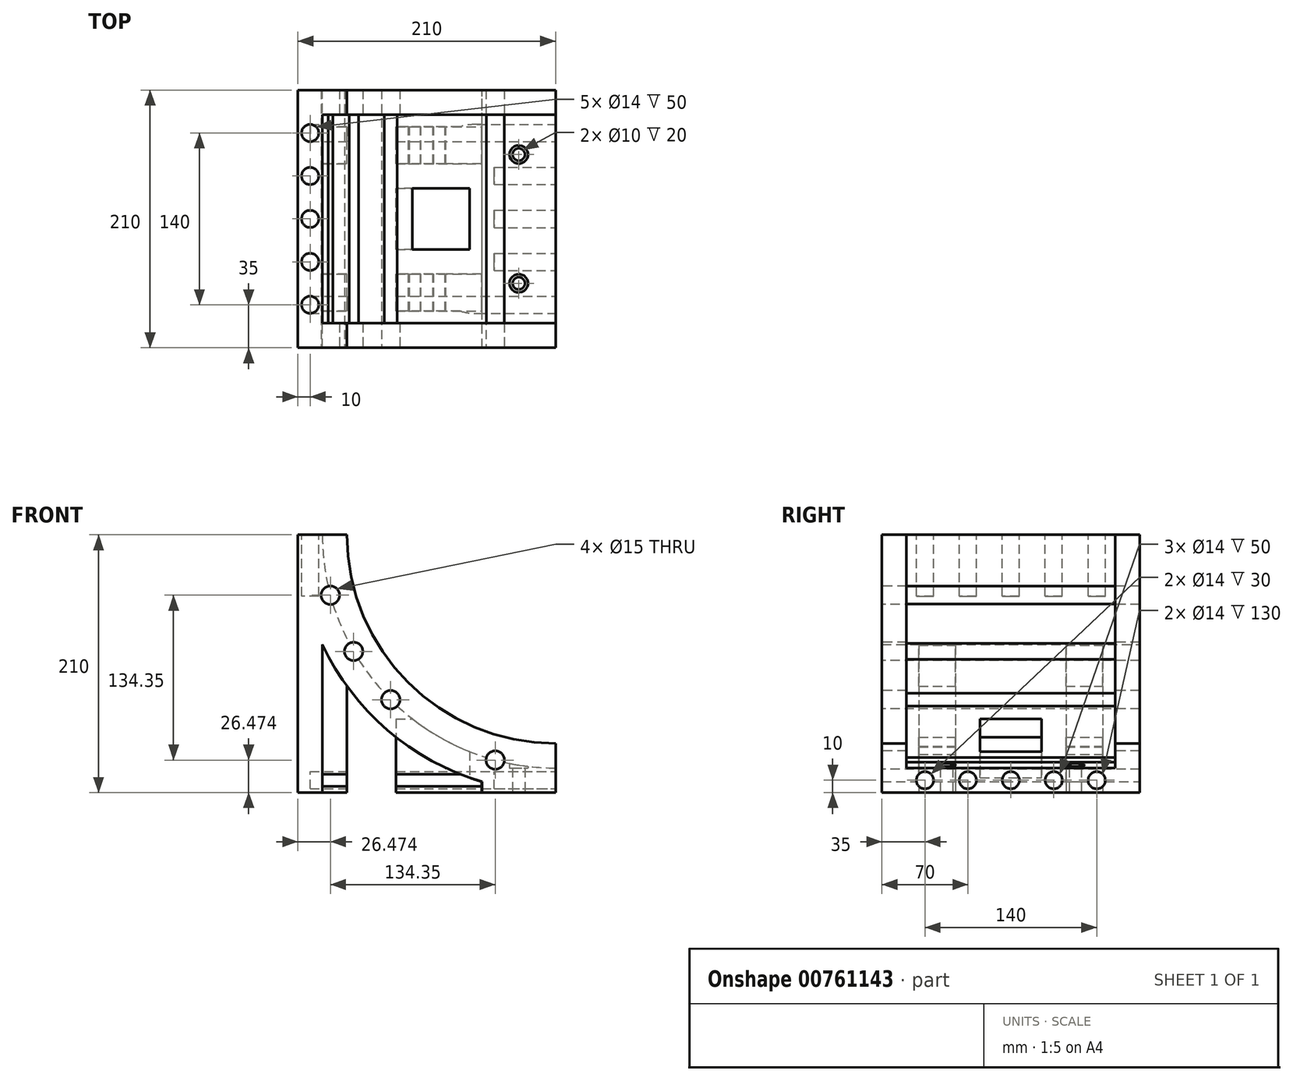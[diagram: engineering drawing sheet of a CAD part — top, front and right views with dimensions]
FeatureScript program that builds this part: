
annotation { "Feature Type Name" : "Feature", "Feature Type Description" : "" }
export const myFeature = defineFeature(function(context is Context, id is Id, definition is map)
    precondition{}
    {
        {
            var Q0;
            Q0=qCreatedBy(makeId("Front.planeOp"),FACE);
            var sketch = newSketch(context, id + "F0", { "sketchPlane" : qUnion([Q0])});
            skCircle(sketch, "E0", {"center": v(0, 0) * mm, "radius": 210 * mm});
            skCircle(sketch, "E1", {"center": v(0, 0) * mm, "radius": 190 * mm});
            skLineSegment(sketch, "E2", {"start": v(0, 0) * mm, "end": v(-210, 0) * mm});
            skLineSegment(sketch, "E3", {"start": v(0, 0) * mm, "end": v(0, -210) * mm});
            skSolve(sketch);
        }
        {
            var Q0;
            {var subQ0=sQuery(id+"F0.wireOp",EDGE,"E2");var subQ1=sQuery(id+"F0.wireOp",EDGE,"E0");var subQ2=makeQuery(id+"F0.imprint","INTERSECT",VERTEX,{"derivedFrom":[subQ1,subQ0]});Q0=makeQuery(id+"F0.imprint","IMPRINT",FACE,{"disambiguationData":[TD([[makeQuery(id+"F0.imprint","IMPRINT",EDGE,{"disambiguationData":[TD([[subQ2,-1.0]])],"derivedFrom":subQ1}),1.0]])]});}
            extrude(context, id + "F1", {"entities" : qUnion([Q0]), "depth" : 210 * mm, "offsetDistance" : 25 * mm});
        }
        {
            var Q0;
            Q0=makeQuery(id+"F1.opExtrude","SWEPT_FACE",FACE,{"disambiguationData":[OSD([sQuery(id+"F0.wireOp",EDGE,"E2")])]});
            extrude(context, id + "F2", {"entities" : qUnion([Q0]), "operationType" : NewBodyOperationType.ADD, "oppositeDirection" : true, "depth" : 210 * mm, "offsetDistance" : 25 * mm});
        }
        {
            var Q0;
            Q0=makeQuery(id+"F1.opExtrude","SWEPT_FACE",FACE,{"disambiguationData":[OSD([sQuery(id+"F0.wireOp",EDGE,"E3")])]});
            extrude(context, id + "F3", {"entities" : qUnion([Q0]), "operationType" : NewBodyOperationType.ADD, "oppositeDirection" : true, "depth" : 60 * mm, "offsetDistance" : 25 * mm});
        }
        {
            var Q0;
            Q0=makeQuery(id+"F3.opExtrude","SWEPT_FACE",FACE,{"disambiguationData":[OSD([sQuery(id+"F0.wireOp",EDGE,"E0"),sQuery(id+"F0.wireOp",EDGE,"E3")])]});
            var sketch = newSketch(context, id + "F4", { "sketchPlane" : qUnion([Q0])});
            skLineSegment(sketch, "E4", {"start": v(-30, 210) * mm, "end": v(-30, 0) * mm});
            skLineSegment(sketch, "E5", {"start": v(0, 157.5) * mm, "end": v(-60, 157.5) * mm});
            skLineSegment(sketch, "E6", {"start": v(-60, 52.5) * mm, "end": v(0, 52.5) * mm});
            skPoint(sketch, "E7", {"position": v(-30, 157.5) * mm});
            skPoint(sketch, "E8", {"position": v(-30, 52.5) * mm});
            skSolve(sketch);
        }
        {
            var Q0;
            Q0=sQuery(id+"F4.wireOp",VERTEX,"E7");
            var Q1;
            Q1=sQuery(id+"F4.wireOp",VERTEX,"E8");
            var Q2;
            Q2=makeQuery(id+"F1.opExtrude","SWEPT_BODY",BODY,{"disambiguationData":[OSD([sQuery(id+"F0.wireOp",EDGE,"E0"),sQuery(id+"F0.wireOp",EDGE,"E1"),sQuery(id+"F0.wireOp",EDGE,"E2"),sQuery(id+"F0.wireOp",EDGE,"E3")])]});
            hole(context, id + "F5", {"style" : HoleStyle.SIMPLE, "endStyle" : HoleEndStyle.BLIND, "holeDiameter" : 15 * mm, "majorDiameter" : 5 * mm, "holeDepth" : 40 * mm, "isTappedThrough" : true, "tappedDepth" : 12 * mm, "tapClearance" : 3, "startFromSketch" : true, "locations" : qUnion([Q0, Q1]), "scope" : qUnion([Q2])});
        }
        {
            var Q0;
            {var subQ0=sQuery(id+"F0.wireOp",EDGE,"E3");var subQ1=sQuery(id+"F0.wireOp",EDGE,"E2");Q0=makeQuery(id+"F3.boolean.opBoolean","MERGE",FACE,{"derivedFrom":[makeQuery(id+"F2.boolean.opBoolean","MERGE",FACE,{"derivedFrom":[makeQuery(id+"F1.opExtrude","CAP_FACE",FACE,{"disambiguationData":[OSD([sQuery(id+"F0.wireOp",EDGE,"E0"),sQuery(id+"F0.wireOp",EDGE,"E1"),subQ1,subQ0])],"isStart":false}),makeQuery(id+"F2.opExtrude","SWEPT_FACE",FACE,{"disambiguationData":[OSD([subQ1]),TDD([makeQuery(id+"F1.opExtrude","CAP_EDGE",EDGE,{"disambiguationData":[OSD([subQ1])],"isStart":false})])]})]}),makeQuery(id+"F3.opExtrude","SWEPT_FACE",FACE,{"disambiguationData":[OSD([subQ0]),TDD([makeQuery(id+"F1.opExtrude","CAP_EDGE",EDGE,{"disambiguationData":[OSD([subQ0])],"isStart":false})])]})]});}
            var sketch = newSketch(context, id + "F6", { "sketchPlane" : qUnion([Q0])});
            skCircle(sketch, "E9", {"center": v(0, 0) * mm, "radius": 170 * mm});
            skLineSegment(sketch, "E10", {"start": v(-190, 0) * mm, "end": v(-170, 0) * mm});
            skLineSegment(sketch, "E11", {"start": v(0, -190) * mm, "end": v(0, -170) * mm});
            skSolve(sketch);
        }
        {
            var Q0;
            {var subQ0=sQuery(id+"F6.wireOp",EDGE,"E10");Q0=makeQuery(id+"F6.imprint","IMPRINT",FACE,{"disambiguationData":[TD([[makeQuery(id+"F6.imprint","IMPRINT",EDGE,{"derivedFrom":subQ0}),-1.0]])]});}
            extrude(context, id + "F7", {"entities" : qUnion([Q0]), "operationType" : NewBodyOperationType.ADD, "oppositeDirection" : true, "depth" : 20 * mm, "offsetDistance" : 25 * mm});
        }
        {
            var Q0;
            {var subQ0=sQuery(id+"F0.wireOp",EDGE,"E3");var subQ1=sQuery(id+"F0.wireOp",EDGE,"E2");Q0=makeQuery(id+"F3.boolean.opBoolean","MERGE",FACE,{"derivedFrom":[makeQuery(id+"F2.boolean.opBoolean","MERGE",FACE,{"derivedFrom":[makeQuery(id+"F1.opExtrude","CAP_FACE",FACE,{"disambiguationData":[OSD([sQuery(id+"F0.wireOp",EDGE,"E0"),sQuery(id+"F0.wireOp",EDGE,"E1"),subQ1,subQ0])],"isStart":true}),makeQuery(id+"F2.opExtrude","SWEPT_FACE",FACE,{"disambiguationData":[OSD([subQ1]),TDD([makeQuery(id+"F1.opExtrude","CAP_EDGE",EDGE,{"disambiguationData":[OSD([subQ1])],"isStart":true})])]})]}),makeQuery(id+"F3.opExtrude","SWEPT_FACE",FACE,{"disambiguationData":[OSD([subQ0]),TDD([makeQuery(id+"F1.opExtrude","CAP_EDGE",EDGE,{"disambiguationData":[OSD([subQ0])],"isStart":true})])]})]});}
            var sketch = newSketch(context, id + "F8", { "sketchPlane" : qUnion([Q0])});
            skCircle(sketch, "E12", {"center": v(0, 0) * mm, "radius": 170 * mm});
            skLineSegment(sketch, "E13", {"start": v(0, -190) * mm, "end": v(0, -170) * mm});
            skLineSegment(sketch, "E14", {"start": v(190, 0) * mm, "end": v(170, 0) * mm});
            skSolve(sketch);
        }
        {
            var Q0;
            {var subQ0=sQuery(id+"F8.wireOp",EDGE,"E13");Q0=makeQuery(id+"F8.imprint","IMPRINT",FACE,{"disambiguationData":[TD([[makeQuery(id+"F8.imprint","IMPRINT",EDGE,{"derivedFrom":subQ0}),-1.0]])]});}
            extrude(context, id + "F9", {"entities" : qUnion([Q0]), "operationType" : NewBodyOperationType.ADD, "oppositeDirection" : true, "depth" : 20 * mm, "offsetDistance" : 25 * mm});
        }
        {
            var Q0;
            {var subQ0=sQuery(id+"F0.wireOp",EDGE,"E1");var subQ1=sQuery(id+"F0.wireOp",EDGE,"E3");var subQ2=sQuery(id+"F0.wireOp",EDGE,"E2");Q0=makeQuery(id+"F7.boolean.opBoolean","MERGE",FACE,{"derivedFrom":[makeQuery(id+"F3.boolean.opBoolean","MERGE",FACE,{"derivedFrom":[makeQuery(id+"F2.boolean.opBoolean","MERGE",FACE,{"derivedFrom":[makeQuery(id+"F1.opExtrude","CAP_FACE",FACE,{"disambiguationData":[OSD([sQuery(id+"F0.wireOp",EDGE,"E0"),subQ0,subQ2,subQ1])],"isStart":false}),makeQuery(id+"F2.opExtrude","SWEPT_FACE",FACE,{"disambiguationData":[OSD([subQ2]),TDD([makeQuery(id+"F1.opExtrude","CAP_EDGE",EDGE,{"disambiguationData":[OSD([subQ2])],"isStart":false})])]})]}),makeQuery(id+"F3.opExtrude","SWEPT_FACE",FACE,{"disambiguationData":[OSD([subQ1]),TDD([makeQuery(id+"F1.opExtrude","CAP_EDGE",EDGE,{"disambiguationData":[OSD([subQ1])],"isStart":false})])]})]}),makeQuery(id+"F7.opExtrude","CAP_FACE",FACE,{"disambiguationData":[OSD([subQ0,sQuery(id+"F6.wireOp",EDGE,"E9"),sQuery(id+"F6.wireOp",EDGE,"E10"),sQuery(id+"F6.wireOp",EDGE,"E11")])],"isStart":true})]});}
            var sketch = newSketch(context, id + "F10", { "sketchPlane" : qUnion([Q0])});
            skLineSegment(sketch, "E15", {"start": v(-30, -210) * mm, "end": v(-30, -167.33) * mm});
            skLineSegment(sketch, "E16", {"start": v(-40, -210) * mm, "end": v(-40, -165.23) * mm});
            skLineSegment(sketch, "E17", {"start": v(-20, -210) * mm, "end": v(-20, -168.82) * mm});
            skLineSegment(sketch, "E18", {"start": v(-40, -190) * mm, "end": v(-20, -190) * mm});
            skSolve(sketch);
        }
        {
            var Q0;
            {var subQ5=sQuery(id+"F10.wireOp",EDGE,"E18");var subQ7=sQuery(id+"F10.wireOp",EDGE,"E16");var subQ9=makeQuery(id+"F10.imprint","INTERSECT",VERTEX,{"derivedFrom":[subQ7,subQ5]});Q0=makeQuery(id+"F10.imprint","IMPRINT",FACE,{"disambiguationData":[TD([[makeQuery(id+"F10.imprint","IMPRINT",EDGE,{"disambiguationData":[TD([[subQ9,-1.0]])],"derivedFrom":subQ5}),-1.0]])]});}
            var Q1;
            {var subQ5=sQuery(id+"F10.wireOp",EDGE,"E18");var subQ7=sQuery(id+"F10.wireOp",EDGE,"E17");var subQ9=makeQuery(id+"F10.imprint","INTERSECT",VERTEX,{"derivedFrom":[subQ7,subQ5]});Q1=makeQuery(id+"F10.imprint","IMPRINT",FACE,{"disambiguationData":[TD([[makeQuery(id+"F10.imprint","IMPRINT",EDGE,{"disambiguationData":[TD([[subQ9,1.0]])],"derivedFrom":subQ5}),-1.0]])]});}
            extrude(context, id + "F11", {"entities" : qUnion([Q0, Q1]), "operationType" : NewBodyOperationType.ADD, "oppositeDirection" : true, "depth" : 210 * mm, "offsetDistance" : 25 * mm});
        }
        {
            var Q0;
            Q0=sQuery(id+"F4.wireOp",VERTEX,"E7");
            var Q1;
            Q1=sQuery(id+"F4.wireOp",VERTEX,"E8");
            var Q2;
            Q2=makeQuery(id+"F1.opExtrude","SWEPT_BODY",BODY,{"disambiguationData":[OSD([sQuery(id+"F0.wireOp",EDGE,"E0"),sQuery(id+"F0.wireOp",EDGE,"E1"),sQuery(id+"F0.wireOp",EDGE,"E2"),sQuery(id+"F0.wireOp",EDGE,"E3")])]});
            hole(context, id + "F12", {"style" : HoleStyle.SIMPLE, "endStyle" : HoleEndStyle.BLIND, "holeDiameter" : 10 * mm, "majorDiameter" : 5 * mm, "holeDepth" : 40 * mm, "isTappedThrough" : true, "tappedDepth" : 12 * mm, "tapClearance" : 3, "startFromSketch" : true, "locations" : qUnion([Q0, Q1]), "scope" : qUnion([Q2])});
        }
        {
            var Q0;
            Q0=makeQuery(id+"F9.boolean.opBoolean","MERGE",FACE,{"derivedFrom":[makeQuery(id+"F7.boolean.opBoolean","MERGE",FACE,{"derivedFrom":[makeQuery(id+"F1.opExtrude","SWEPT_FACE",FACE,{"disambiguationData":[OSD([sQuery(id+"F0.wireOp",EDGE,"E3")])]}),makeQuery(id+"F7.opExtrude","SWEPT_FACE",FACE,{"disambiguationData":[OSD([sQuery(id+"F6.wireOp",EDGE,"E11")])]})]}),makeQuery(id+"F9.opExtrude","SWEPT_FACE",FACE,{"disambiguationData":[OSD([sQuery(id+"F8.wireOp",EDGE,"E13")])]})]});
            var sketch = newSketch(context, id + "F13", { "sketchPlane" : qUnion([Q0])});
            skLineSegment(sketch, "E19", {"start": v(-175, -190) * mm, "end": v(-175, -210) * mm, "construction": true});
            skLineSegment(sketch, "E20", {"start": v(-140, -190) * mm, "end": v(-140, -210) * mm, "construction": true});
            skLineSegment(sketch, "E21", {"start": v(-105, -190) * mm, "end": v(-105, -210) * mm, "construction": true});
            skLineSegment(sketch, "E22", {"start": v(-70, -190) * mm, "end": v(-70, -210) * mm, "construction": true});
            skLineSegment(sketch, "E23", {"start": v(-35, -190) * mm, "end": v(-35, -210) * mm, "construction": true});
            skPoint(sketch, "E24", {"position": v(-175, -200) * mm});
            skPoint(sketch, "E25", {"position": v(-140, -200) * mm});
            skPoint(sketch, "E26", {"position": v(-105, -200) * mm});
            skPoint(sketch, "E27", {"position": v(-70, -200) * mm});
            skPoint(sketch, "E28", {"position": v(-35, -200) * mm});
            skCircle(sketch, "E29", {"center": v(-35, -200) * mm, "radius": 7 * mm});
            skCircle(sketch, "E30", {"center": v(-105, -200) * mm, "radius": 7 * mm});
            skCircle(sketch, "E31", {"center": v(-70, -200) * mm, "radius": 7 * mm});
            skCircle(sketch, "E32", {"center": v(-140, -200) * mm, "radius": 7 * mm});
            skCircle(sketch, "E33", {"center": v(-175, -200) * mm, "radius": 7 * mm});
            skSolve(sketch);
        }
        {
            var Q0;
            Q0=makeQuery(id+"F13.imprint","IMPRINT",FACE,{"disambiguationData":[TD([[makeQuery(id+"F13.imprint","IMPRINT",EDGE,{"derivedFrom":sQuery(id+"F13.wireOp",EDGE,"E32")}),1.0]])]});
            var Q1;
            Q1=makeQuery(id+"F13.imprint","IMPRINT",FACE,{"disambiguationData":[TD([[makeQuery(id+"F13.imprint","IMPRINT",EDGE,{"derivedFrom":sQuery(id+"F13.wireOp",EDGE,"E30")}),1.0]])]});
            var Q2;
            Q2=makeQuery(id+"F13.imprint","IMPRINT",FACE,{"disambiguationData":[TD([[makeQuery(id+"F13.imprint","IMPRINT",EDGE,{"derivedFrom":sQuery(id+"F13.wireOp",EDGE,"E31")}),1.0]])]});
            extrude(context, id + "F14", {"entities" : qUnion([Q0, Q1, Q2]), "operationType" : NewBodyOperationType.REMOVE, "oppositeDirection" : true, "depth" : 50 * mm, "offsetDistance" : 25 * mm});
        }
        {
            var Q0;
            Q0=makeQuery(id+"F9.boolean.opBoolean","MERGE",FACE,{"derivedFrom":[makeQuery(id+"F7.boolean.opBoolean","MERGE",FACE,{"derivedFrom":[makeQuery(id+"F1.opExtrude","SWEPT_FACE",FACE,{"disambiguationData":[OSD([sQuery(id+"F0.wireOp",EDGE,"E2")])]}),makeQuery(id+"F7.opExtrude","SWEPT_FACE",FACE,{"disambiguationData":[OSD([sQuery(id+"F6.wireOp",EDGE,"E10")])]})]}),makeQuery(id+"F9.opExtrude","SWEPT_FACE",FACE,{"disambiguationData":[OSD([sQuery(id+"F8.wireOp",EDGE,"E14")])]})]});
            var sketch = newSketch(context, id + "F15", { "sketchPlane" : qUnion([Q0])});
            skLineSegment(sketch, "E34", {"start": v(-190, -35) * mm, "end": v(-210, -35) * mm, "construction": true});
            skLineSegment(sketch, "E35", {"start": v(-190, -70) * mm, "end": v(-210, -70) * mm, "construction": true});
            skLineSegment(sketch, "E36", {"start": v(-190, -105) * mm, "end": v(-210, -105) * mm, "construction": true});
            skLineSegment(sketch, "E37", {"start": v(-190, -140) * mm, "end": v(-210, -140) * mm, "construction": true});
            skLineSegment(sketch, "E38", {"start": v(-190, -175) * mm, "end": v(-210, -175) * mm, "construction": true});
            skLineSegment(sketch, "E39", {"start": v(-200, -35) * mm, "end": v(-200, -175) * mm, "construction": true});
            skCircle(sketch, "E40", {"center": v(-200, -35) * mm, "radius": 7 * mm});
            skCircle(sketch, "E41", {"center": v(-200, -70) * mm, "radius": 7 * mm});
            skCircle(sketch, "E42", {"center": v(-200, -105) * mm, "radius": 7 * mm});
            skCircle(sketch, "E43", {"center": v(-200, -140) * mm, "radius": 7 * mm});
            skCircle(sketch, "E44", {"center": v(-200, -175) * mm, "radius": 7 * mm});
            skSolve(sketch);
        }
        {
            var Q0;
            Q0=makeQuery(id+"F15.imprint","IMPRINT",FACE,{"disambiguationData":[TD([[makeQuery(id+"F15.imprint","IMPRINT",EDGE,{"derivedFrom":sQuery(id+"F15.wireOp",EDGE,"E40")}),1.0]])]});
            var Q1;
            Q1=makeQuery(id+"F15.imprint","IMPRINT",FACE,{"disambiguationData":[TD([[makeQuery(id+"F15.imprint","IMPRINT",EDGE,{"derivedFrom":sQuery(id+"F15.wireOp",EDGE,"E41")}),1.0]])]});
            var Q2;
            Q2=makeQuery(id+"F15.imprint","IMPRINT",FACE,{"disambiguationData":[TD([[makeQuery(id+"F15.imprint","IMPRINT",EDGE,{"derivedFrom":sQuery(id+"F15.wireOp",EDGE,"E42")}),1.0]])]});
            var Q3;
            Q3=makeQuery(id+"F15.imprint","IMPRINT",FACE,{"disambiguationData":[TD([[makeQuery(id+"F15.imprint","IMPRINT",EDGE,{"derivedFrom":sQuery(id+"F15.wireOp",EDGE,"E43")}),1.0]])]});
            var Q4;
            Q4=makeQuery(id+"F15.imprint","IMPRINT",FACE,{"disambiguationData":[TD([[makeQuery(id+"F15.imprint","IMPRINT",EDGE,{"derivedFrom":sQuery(id+"F15.wireOp",EDGE,"E44")}),1.0]])]});
            extrude(context, id + "F16", {"entities" : qUnion([Q0, Q1, Q2, Q3, Q4]), "operationType" : NewBodyOperationType.REMOVE, "oppositeDirection" : true, "depth" : 50 * mm, "offsetDistance" : 25 * mm});
        }
        {
            var Q0;
            {var subQ0=sQuery(id+"F0.wireOp",EDGE,"E1");var subQ1=sQuery(id+"F0.wireOp",EDGE,"E3");var subQ2=sQuery(id+"F0.wireOp",EDGE,"E2");Q0=makeQuery(id+"F7.boolean.opBoolean","MERGE",FACE,{"derivedFrom":[makeQuery(id+"F3.boolean.opBoolean","MERGE",FACE,{"derivedFrom":[makeQuery(id+"F2.boolean.opBoolean","MERGE",FACE,{"derivedFrom":[makeQuery(id+"F1.opExtrude","CAP_FACE",FACE,{"disambiguationData":[OSD([sQuery(id+"F0.wireOp",EDGE,"E0"),subQ0,subQ2,subQ1])],"isStart":false}),makeQuery(id+"F2.opExtrude","SWEPT_FACE",FACE,{"disambiguationData":[OSD([subQ2]),TDD([makeQuery(id+"F1.opExtrude","CAP_EDGE",EDGE,{"disambiguationData":[OSD([subQ2])],"isStart":false})])]})]}),makeQuery(id+"F3.opExtrude","SWEPT_FACE",FACE,{"disambiguationData":[OSD([subQ1]),TDD([makeQuery(id+"F1.opExtrude","CAP_EDGE",EDGE,{"disambiguationData":[OSD([subQ1])],"isStart":false})])]})]}),makeQuery(id+"F7.opExtrude","CAP_FACE",FACE,{"disambiguationData":[OSD([subQ0,sQuery(id+"F6.wireOp",EDGE,"E9"),sQuery(id+"F6.wireOp",EDGE,"E10"),sQuery(id+"F6.wireOp",EDGE,"E11")])],"isStart":true})]});}
            var sketch = newSketch(context, id + "F17", { "sketchPlane" : qUnion([Q0])});
            skCircle(sketch, "E45", {"center": v(0, 0) * mm, "radius": 190 * mm});
            skLineSegment(sketch, "E46", {"start": v(0, 0) * mm, "end": v(-183.53, -49.18) * mm, "construction": true});
            skLineSegment(sketch, "E47", {"start": v(0, 0) * mm, "end": v(-49.18, -183.53) * mm, "construction": true});
            skLineSegment(sketch, "E48", {"start": v(0, 0) * mm, "end": v(-164.54, -95) * mm, "construction": true});
            skLineSegment(sketch, "E49", {"start": v(0, 0) * mm, "end": v(-95, -164.54) * mm, "construction": true});
            skLineSegment(sketch, "E50", {"start": v(0, 0) * mm, "end": v(-134.35, -134.35) * mm, "construction": true});
            skPoint(sketch, "E51", {"position": v(-183.53, -49.18) * mm});
            skPoint(sketch, "E52", {"position": v(-164.54, -95) * mm});
            skPoint(sketch, "E53", {"position": v(-134.35, -134.35) * mm});
            skPoint(sketch, "E54", {"position": v(-49.18, -183.53) * mm});
            skSolve(sketch);
        }
        {
            var Q0;
            Q0=sQuery(id+"F17.wireOp",VERTEX,"E51");
            var Q1;
            Q1=sQuery(id+"F17.wireOp",VERTEX,"E52");
            var Q2;
            Q2=sQuery(id+"F17.wireOp",VERTEX,"E53");
            var Q3;
            Q3=sQuery(id+"F17.wireOp",VERTEX,"E54");
            var Q4;
            Q4=makeQuery(id+"F1.opExtrude","SWEPT_BODY",BODY,{"disambiguationData":[OSD([sQuery(id+"F0.wireOp",EDGE,"E0"),sQuery(id+"F0.wireOp",EDGE,"E1"),sQuery(id+"F0.wireOp",EDGE,"E2"),sQuery(id+"F0.wireOp",EDGE,"E3")])]});
            hole(context, id + "F18", {"style" : HoleStyle.SIMPLE, "endStyle" : HoleEndStyle.BLIND, "holeDiameter" : 15 * mm, "majorDiameter" : 5 * mm, "holeDepth" : 220 * mm, "isTappedThrough" : true, "tappedDepth" : 12 * mm, "tapClearance" : 3, "startFromSketch" : true, "locations" : qUnion([Q0, Q1, Q2, Q3]), "scope" : qUnion([Q4])});
        }
        {
            var Q0;
            Q0=makeQuery(id+"F2.opExtrude","CAP_FACE",FACE,{"disambiguationData":[OSD([sQuery(id+"F0.wireOp",EDGE,"E2")])],"isStart":false});
            var sketch = newSketch(context, id + "F19", { "sketchPlane" : qUnion([Q0])});
            skLineSegment(sketch, "E55", {"start": v(-190, 130) * mm, "end": v(-60.32, 130) * mm});
            skLineSegment(sketch, "E56", {"start": v(-190, 80) * mm, "end": v(-59.02, 80) * mm});
            skLineSegment(sketch, "E57", {"start": v(-70, 130) * mm, "end": v(-70, 80) * mm});
            skLineSegment(sketch, "E58", {"start": v(-130, 80) * mm, "end": v(-130, 130) * mm});
            skSolve(sketch);
        }
        {
            var Q0;
            {var subQ0=sQuery(id+"F19.wireOp",EDGE,"E57");Q0=makeQuery(id+"F19.imprint","IMPRINT",FACE,{"disambiguationData":[TD([[makeQuery(id+"F19.imprint","IMPRINT",EDGE,{"derivedFrom":subQ0}),-1.0]])]});}
            extrude(context, id + "F20", {"entities" : qUnion([Q0]), "operationType" : NewBodyOperationType.REMOVE, "oppositeDirection" : true, "depth" : 60 * mm, "offsetDistance" : 25 * mm});
        }
        {
            var Q0;
            Q0=makeQuery(id+"F2.opExtrude","CAP_FACE",FACE,{"disambiguationData":[OSD([sQuery(id+"F0.wireOp",EDGE,"E2")])],"isStart":false});
            var sketch = newSketch(context, id + "F21", { "sketchPlane" : qUnion([Q0])});
            skLineSegment(sketch, "E59", {"start": v(-190, 180) * mm, "end": v(-30, 180) * mm});
            skLineSegment(sketch, "E60", {"start": v(-190, 150) * mm, "end": v(-30, 150) * mm});
            skLineSegment(sketch, "E61", {"start": v(-190, 60) * mm, "end": v(-59.68, 60) * mm});
            skLineSegment(sketch, "E62", {"start": v(-190, 30) * mm, "end": v(-60.34, 30) * mm});
            skLineSegment(sketch, "E63", {"start": v(-70, 180) * mm, "end": v(-70, 150) * mm});
            skLineSegment(sketch, "E64", {"start": v(-80, 180) * mm, "end": v(-80, 150) * mm});
            skLineSegment(sketch, "E65", {"start": v(-90, 180) * mm, "end": v(-90, 150) * mm});
            skLineSegment(sketch, "E66", {"start": v(-160, 180) * mm, "end": v(-160, 150) * mm});
            skLineSegment(sketch, "E67", {"start": v(-140, 180) * mm, "end": v(-140, 150) * mm});
            skLineSegment(sketch, "E68", {"start": v(-130, 180) * mm, "end": v(-130, 150) * mm});
            skLineSegment(sketch, "E69", {"start": v(-120, 180) * mm, "end": v(-120, 150) * mm});
            skLineSegment(sketch, "E70", {"start": v(-100, 180) * mm, "end": v(-100, 150) * mm});
            skLineSegment(sketch, "E71", {"start": v(-110, 180) * mm, "end": v(-110, 150) * mm});
            skLineSegment(sketch, "E72", {"start": v(-150, 150) * mm, "end": v(-150, 180) * mm});
            skLineSegment(sketch, "E73", {"start": v(-170, 180) * mm, "end": v(-170, 150) * mm});
            skLineSegment(sketch, "E74", {"start": v(-180, 180) * mm, "end": v(-180, 150) * mm});
            skLineSegment(sketch, "E75", {"start": v(-140, 60) * mm, "end": v(-140, 30) * mm});
            skLineSegment(sketch, "E76", {"start": v(-70, 60) * mm, "end": v(-70, 30) * mm});
            skLineSegment(sketch, "E77", {"start": v(-80, 60) * mm, "end": v(-80, 30) * mm});
            skLineSegment(sketch, "E78", {"start": v(-90, 60) * mm, "end": v(-90, 30) * mm});
            skLineSegment(sketch, "E79", {"start": v(-100, 60) * mm, "end": v(-100, 30) * mm});
            skLineSegment(sketch, "E80", {"start": v(-110, 60) * mm, "end": v(-110, 30) * mm});
            skLineSegment(sketch, "E81", {"start": v(-120, 60) * mm, "end": v(-120, 30) * mm});
            skLineSegment(sketch, "E82", {"start": v(-130, 60) * mm, "end": v(-130, 30) * mm});
            skLineSegment(sketch, "E83", {"start": v(-150, 60) * mm, "end": v(-150, 30) * mm});
            skLineSegment(sketch, "E84", {"start": v(-160, 30) * mm, "end": v(-160, 60) * mm});
            skLineSegment(sketch, "E85", {"start": v(-170, 30) * mm, "end": v(-170, 60) * mm});
            skLineSegment(sketch, "E86", {"start": v(-180, 60) * mm, "end": v(-180, 30) * mm});
            skLineSegment(sketch, "E87", {"start": v(-60.34, 30) * mm, "end": v(-60.34, 180) * mm});
            skSolve(sketch);
        }
        {
            var Q0;
            {var subQ0=sQuery(id+"F21.wireOp",EDGE,"E76");Q0=makeQuery(id+"F21.imprint","IMPRINT",FACE,{"disambiguationData":[TD([[makeQuery(id+"F21.imprint","IMPRINT",EDGE,{"derivedFrom":subQ0}),1.0]])]});}
            var Q1;
            {var subQ0=sQuery(id+"F21.wireOp",EDGE,"E63");Q1=makeQuery(id+"F21.imprint","IMPRINT",FACE,{"disambiguationData":[TD([[makeQuery(id+"F21.imprint","IMPRINT",EDGE,{"derivedFrom":subQ0}),-1.0]])]});}
            var Q2;
            {var subQ0=sQuery(id+"F21.wireOp",EDGE,"E63");Q2=makeQuery(id+"F21.imprint","IMPRINT",FACE,{"disambiguationData":[TD([[makeQuery(id+"F21.imprint","IMPRINT",EDGE,{"derivedFrom":subQ0}),1.0]])]});}
            var Q3;
            {var subQ0=sQuery(id+"F21.wireOp",EDGE,"E76");Q3=makeQuery(id+"F21.imprint","IMPRINT",FACE,{"disambiguationData":[TD([[makeQuery(id+"F21.imprint","IMPRINT",EDGE,{"derivedFrom":subQ0}),-1.0]])]});}
            var Q4;
            {var subQ0=sQuery(id+"F21.wireOp",EDGE,"E64");Q4=makeQuery(id+"F21.imprint","IMPRINT",FACE,{"disambiguationData":[TD([[makeQuery(id+"F21.imprint","IMPRINT",EDGE,{"derivedFrom":subQ0}),-1.0]])]});}
            var Q5;
            {var subQ0=sQuery(id+"F21.wireOp",EDGE,"E77");Q5=makeQuery(id+"F21.imprint","IMPRINT",FACE,{"disambiguationData":[TD([[makeQuery(id+"F21.imprint","IMPRINT",EDGE,{"derivedFrom":subQ0}),-1.0]])]});}
            extrude(context, id + "F22", {"entities" : qUnion([Q0, Q1, Q2, Q3, Q4, Q5]), "operationType" : NewBodyOperationType.ADD, "oppositeDirection" : true, "depth" : 20 * mm, "offsetDistance" : 25 * mm});
        }
        {
            var Q0;
            {var subQ0=sQuery(id+"F21.wireOp",EDGE,"E65");Q0=makeQuery(id+"F21.imprint","IMPRINT",FACE,{"disambiguationData":[TD([[makeQuery(id+"F21.imprint","IMPRINT",EDGE,{"derivedFrom":subQ0}),-1.0]])]});}
            var Q1;
            {var subQ0=sQuery(id+"F21.wireOp",EDGE,"E78");Q1=makeQuery(id+"F21.imprint","IMPRINT",FACE,{"disambiguationData":[TD([[makeQuery(id+"F21.imprint","IMPRINT",EDGE,{"derivedFrom":subQ0}),-1.0]])]});}
            extrude(context, id + "F23", {"entities" : qUnion([Q0, Q1]), "operationType" : NewBodyOperationType.ADD, "oppositeDirection" : true, "depth" : 25 * mm, "offsetDistance" : 25 * mm});
        }
        {
            var Q0;
            {var subQ0=sQuery(id+"F21.wireOp",EDGE,"E70");Q0=makeQuery(id+"F21.imprint","IMPRINT",FACE,{"disambiguationData":[TD([[makeQuery(id+"F21.imprint","IMPRINT",EDGE,{"derivedFrom":subQ0}),-1.0]])]});}
            var Q1;
            {var subQ0=sQuery(id+"F21.wireOp",EDGE,"E79");Q1=makeQuery(id+"F21.imprint","IMPRINT",FACE,{"disambiguationData":[TD([[makeQuery(id+"F21.imprint","IMPRINT",EDGE,{"derivedFrom":subQ0}),-1.0]])]});}
            extrude(context, id + "F24", {"entities" : qUnion([Q0, Q1]), "operationType" : NewBodyOperationType.ADD, "oppositeDirection" : true, "depth" : 31 * mm, "offsetDistance" : 25 * mm});
        }
        {
            var Q0;
            {var subQ0=sQuery(id+"F21.wireOp",EDGE,"E69");Q0=makeQuery(id+"F21.imprint","IMPRINT",FACE,{"disambiguationData":[TD([[makeQuery(id+"F21.imprint","IMPRINT",EDGE,{"derivedFrom":subQ0}),1.0]])]});}
            var Q1;
            {var subQ0=sQuery(id+"F21.wireOp",EDGE,"E80");Q1=makeQuery(id+"F21.imprint","IMPRINT",FACE,{"disambiguationData":[TD([[makeQuery(id+"F21.imprint","IMPRINT",EDGE,{"derivedFrom":subQ0}),-1.0]])]});}
            extrude(context, id + "F25", {"entities" : qUnion([Q0, Q1]), "operationType" : NewBodyOperationType.ADD, "oppositeDirection" : true, "depth" : 37 * mm, "offsetDistance" : 25 * mm});
        }
        {
            var Q0;
            {var subQ0=sQuery(id+"F21.wireOp",EDGE,"E81");Q0=makeQuery(id+"F21.imprint","IMPRINT",FACE,{"disambiguationData":[TD([[makeQuery(id+"F21.imprint","IMPRINT",EDGE,{"derivedFrom":subQ0}),-1.0]])]});}
            var Q1;
            {var subQ0=sQuery(id+"F21.wireOp",EDGE,"E68");Q1=makeQuery(id+"F21.imprint","IMPRINT",FACE,{"disambiguationData":[TD([[makeQuery(id+"F21.imprint","IMPRINT",EDGE,{"derivedFrom":subQ0}),1.0]])]});}
            extrude(context, id + "F26", {"entities" : qUnion([Q0, Q1]), "operationType" : NewBodyOperationType.ADD, "oppositeDirection" : true, "depth" : 45 * mm, "offsetDistance" : 25 * mm});
        }
        {
            var Q0;
            {var subQ3=sQuery(id+"F21.wireOp",EDGE,"E74");Q0=makeQuery(id+"F21.imprint","IMPRINT",FACE,{"disambiguationData":[TD([[makeQuery(id+"F21.imprint","IMPRINT",EDGE,{"derivedFrom":subQ3}),-1.0]])]});}
            var Q1;
            {var subQ3=sQuery(id+"F21.wireOp",EDGE,"E86");Q1=makeQuery(id+"F21.imprint","IMPRINT",FACE,{"disambiguationData":[TD([[makeQuery(id+"F21.imprint","IMPRINT",EDGE,{"derivedFrom":subQ3}),-1.0]])]});}
            extrude(context, id + "F27", {"entities" : qUnion([Q0, Q1]), "operationType" : NewBodyOperationType.ADD, "oppositeDirection" : true, "depth" : 120 * mm, "offsetDistance" : 25 * mm});
        }
        {
            var Q0;
            {var subQ0=sQuery(id+"F21.wireOp",EDGE,"E73");Q0=makeQuery(id+"F21.imprint","IMPRINT",FACE,{"disambiguationData":[TD([[makeQuery(id+"F21.imprint","IMPRINT",EDGE,{"derivedFrom":subQ0}),-1.0]])]});}
            var Q1;
            {var subQ0=sQuery(id+"F21.wireOp",EDGE,"E85");Q1=makeQuery(id+"F21.imprint","IMPRINT",FACE,{"disambiguationData":[TD([[makeQuery(id+"F21.imprint","IMPRINT",EDGE,{"derivedFrom":subQ0}),1.0]])]});}
            extrude(context, id + "F28", {"entities" : qUnion([Q0, Q1]), "operationType" : NewBodyOperationType.ADD, "oppositeDirection" : true, "depth" : 105 * mm, "offsetDistance" : 25 * mm});
        }
        {
            var Q0;
            Q0=makeQuery(id+"F13.imprint","IMPRINT",FACE,{"disambiguationData":[TD([[makeQuery(id+"F13.imprint","IMPRINT",EDGE,{"derivedFrom":sQuery(id+"F13.wireOp",EDGE,"E29")}),1.0]])]});
            var Q1;
            Q1=makeQuery(id+"F13.imprint","IMPRINT",FACE,{"disambiguationData":[TD([[makeQuery(id+"F13.imprint","IMPRINT",EDGE,{"derivedFrom":sQuery(id+"F13.wireOp",EDGE,"E33")}),1.0]])]});
            extrude(context, id + "F29", {"entities" : qUnion([Q0, Q1]), "operationType" : NewBodyOperationType.REMOVE, "oppositeDirection" : true, "depth" : 200 * mm, "offsetDistance" : 25 * mm});
        }
    });
